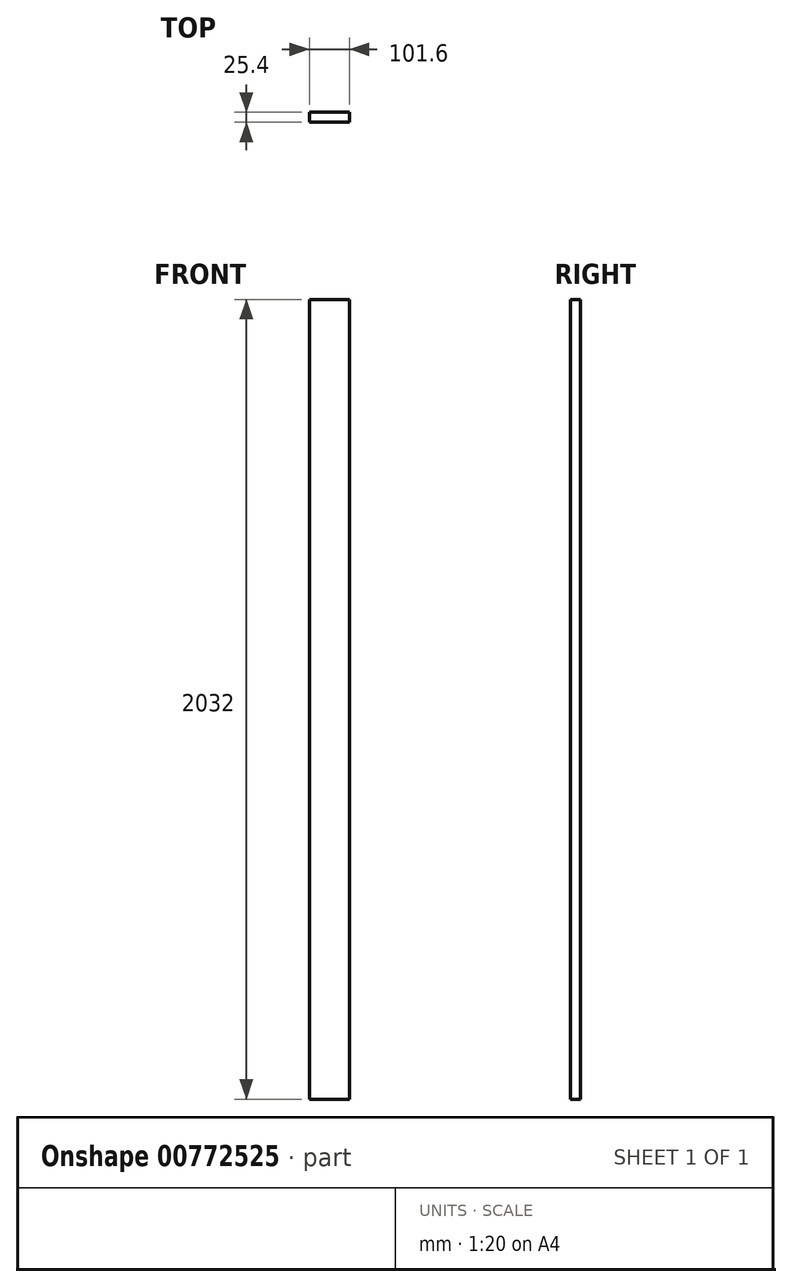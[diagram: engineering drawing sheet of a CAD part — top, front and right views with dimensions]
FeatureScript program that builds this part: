
annotation { "Feature Type Name" : "Feature", "Feature Type Description" : "" }
export const myFeature = defineFeature(function(context is Context, id is Id, definition is map)
    precondition{}
    {
        {
            var Q0;
            Q0=qCreatedBy(makeId("Front.planeOp"),FACE);
            var sketch = newSketch(context, id + "F0", { "sketchPlane" : qUnion([Q0])});
            skLineSegment(sketch, "E0.bottom", {"start": v(-50.8, 1016) * mm, "end": v(50.8, 1016) * mm});
            skLineSegment(sketch, "E0.top", {"start": v(-50.8, -1016) * mm, "end": v(50.8, -1016) * mm});
            skLineSegment(sketch, "E0.left", {"start": v(-50.8, 1016) * mm, "end": v(-50.8, -1016) * mm});
            skLineSegment(sketch, "E0.right", {"start": v(50.8, 1016) * mm, "end": v(50.8, -1016) * mm});
            skSolve(sketch);
        }
        {
            var Q0;
            Q0 = qSketchRegion(id + "F0", true);
            extrude(context, id + "F1", {"entities" : qUnion([Q0]), "oppositeDirection" : true, "depth" : 25.4 * mm, "offsetDistance" : 25.4 * mm});
        }
    });
